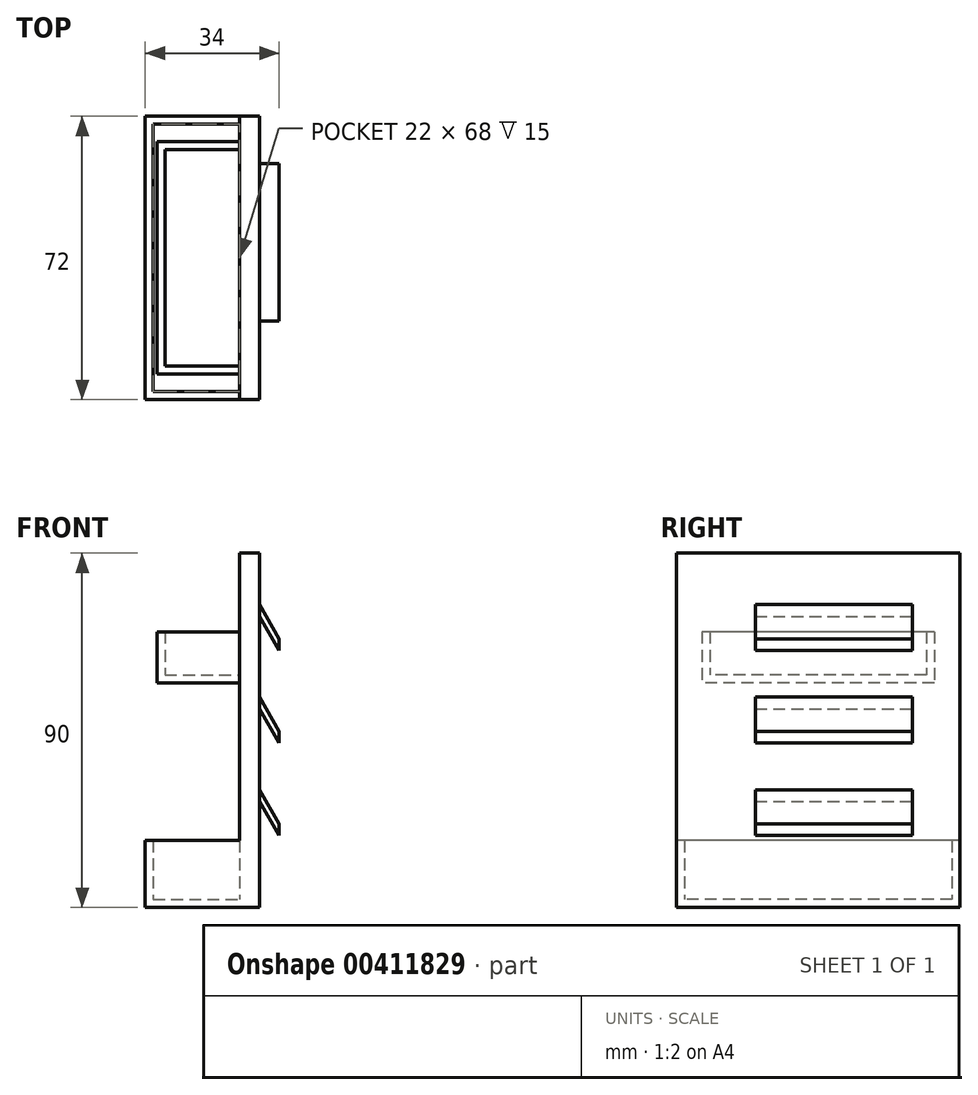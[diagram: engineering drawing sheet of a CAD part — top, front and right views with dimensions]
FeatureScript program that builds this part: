
annotation { "Feature Type Name" : "Feature", "Feature Type Description" : "" }
export const myFeature = defineFeature(function(context is Context, id is Id, definition is map)
    precondition{}
    {
        {
            var Q0;
            Q0=qCreatedBy(makeId("Top.planeOp"),FACE);
            var sketch = newSketch(context, id + "F0", { "sketchPlane" : qUnion([Q0])});
            skLineSegment(sketch, "E0.bottom", {"start": v(2.5, 36) * mm, "end": v(-2.5, 36) * mm});
            skLineSegment(sketch, "E0.top", {"start": v(2.5, -36) * mm, "end": v(-2.5, -36) * mm});
            skLineSegment(sketch, "E0.left", {"start": v(2.5, 36) * mm, "end": v(2.5, -36) * mm});
            skLineSegment(sketch, "E0.right", {"start": v(-2.5, 36) * mm, "end": v(-2.5, -36) * mm});
            skPoint(sketch, "E0.middle", {"position": v(0, 0) * mm});
            skLineSegment(sketch, "E1", {"start": v(-2.5, 36) * mm, "end": v(-26.5, 36) * mm});
            skLineSegment(sketch, "E2", {"start": v(-26.5, 36) * mm, "end": v(-26.5, -36) * mm});
            skLineSegment(sketch, "E3", {"start": v(-26.5, -36) * mm, "end": v(-2.5, -36) * mm});
            skLineSegment(sketch, "E4.0", {"start": v(-24.5, -34) * mm, "end": v(-2.5, -34) * mm});
            skLineSegment(sketch, "E4.1", {"start": v(-24.5, 34) * mm, "end": v(-24.5, -34) * mm});
            skLineSegment(sketch, "E4.2", {"start": v(-2.5, 34) * mm, "end": v(-24.5, 34) * mm});
            skSolve(sketch);
        }
        {
            var Q0;
            Q0=makeQuery(id+"F0.imprint","IMPRINT",FACE,{"disambiguationData":[TD([[makeQuery(id+"F0.imprint","IMPRINT",EDGE,{"derivedFrom":sQuery(id+"F0.wireOp",EDGE,"E0.bottom")}),1.0]])]});
            extrude(context, id + "F1", {"entities" : qUnion([Q0]), "depth" : 90 * mm});
        }
        {
            var Q0;
            {var subQ0=sQuery(id+"F0.wireOp",EDGE,"E1");Q0=makeQuery(id+"F0.imprint","IMPRINT",FACE,{"disambiguationData":[TD([[makeQuery(id+"F0.imprint","IMPRINT",EDGE,{"derivedFrom":subQ0}),1.0]])]});}
            extrude(context, id + "F2", {"entities" : qUnion([Q0]), "operationType" : NewBodyOperationType.ADD, "depth" : 17 * mm});
        }
        {
            var Q0;
            {var subQ0=sQuery(id+"F0.wireOp",EDGE,"E4.0");Q0=makeQuery(id+"F0.imprint","IMPRINT",FACE,{"disambiguationData":[TD([[makeQuery(id+"F0.imprint","IMPRINT",EDGE,{"derivedFrom":subQ0}),1.0]])]});}
            extrude(context, id + "F3", {"entities" : qUnion([Q0]), "operationType" : NewBodyOperationType.ADD, "depth" : 2 * mm});
        }
        {
            var Q0;
            Q0=makeQuery(id+"F2.opExtrude","CAP_FACE",FACE,{"disambiguationData":[OSD([sQuery(id+"F0.wireOp",EDGE,"E0.right"),sQuery(id+"F0.wireOp",EDGE,"E1"),sQuery(id+"F0.wireOp",EDGE,"E2"),sQuery(id+"F0.wireOp",EDGE,"E3"),sQuery(id+"F0.wireOp",EDGE,"E4.0"),sQuery(id+"F0.wireOp",EDGE,"E4.1"),sQuery(id+"F0.wireOp",EDGE,"E4.2")])],"isStart":false});
            cPlane(context, id + "F4", {"entities" : qUnion([Q0]), "cplaneType" : CPlaneType.OFFSET, "offset" : 40 * mm, "width" : 150 * mm, "height" : 150 * mm});
        }
        {
            var Q0;
            Q0=qCreatedBy(id+"F4.planeOp",FACE);
            var sketch = newSketch(context, id + "F5", { "sketchPlane" : qUnion([Q0])});
            skLineSegment(sketch, "E5.0", {"start": v(-2.5, 36) * mm, "end": v(-2.5, -36) * mm});
            skPoint(sketch, "E6.0", {"position": v(-2.5, 0) * mm});
            skLineSegment(sketch, "E7", {"start": v(-2.5, 29.5) * mm, "end": v(-23.5, 29.5) * mm});
            skLineSegment(sketch, "E8", {"start": v(-23.5, 29.5) * mm, "end": v(-23.5, -29.5) * mm});
            skLineSegment(sketch, "E9", {"start": v(-23.5, -29.5) * mm, "end": v(-2.5, -29.5) * mm});
            skLineSegment(sketch, "E10.0", {"start": v(-21.5, -27.5) * mm, "end": v(-2.5, -27.5) * mm});
            skLineSegment(sketch, "E10.1", {"start": v(-21.5, 27.5) * mm, "end": v(-21.5, -27.5) * mm});
            skLineSegment(sketch, "E10.2", {"start": v(-2.5, 27.5) * mm, "end": v(-21.5, 27.5) * mm});
            skPoint(sketch, "E11", {"position": v(-21.5, 0) * mm});
            skSolve(sketch);
        }
        {
            var Q0;
            {var subQ0=sQuery(id+"F5.wireOp",EDGE,"E7");Q0=makeQuery(id+"F5.imprint","IMPRINT",FACE,{"disambiguationData":[TD([[makeQuery(id+"F5.imprint","IMPRINT",EDGE,{"derivedFrom":subQ0}),1.0]])]});}
            extrude(context, id + "F6", {"entities" : qUnion([Q0]), "operationType" : NewBodyOperationType.ADD, "depth" : 13 * mm});
        }
        {
            var Q0;
            {var subQ0=sQuery(id+"F5.wireOp",EDGE,"E10.0");Q0=makeQuery(id+"F5.imprint","IMPRINT",FACE,{"disambiguationData":[TD([[makeQuery(id+"F5.imprint","IMPRINT",EDGE,{"derivedFrom":subQ0}),1.0]])]});}
            extrude(context, id + "F7", {"entities" : qUnion([Q0]), "operationType" : NewBodyOperationType.ADD, "depth" : 2 * mm});
        }
        {
            var Q0;
            Q0=makeQuery(id+"F2.boolean.opBoolean","MERGE",FACE,{"derivedFrom":[makeQuery(id+"F1.opExtrude","SWEPT_FACE",FACE,{"disambiguationData":[OSD([sQuery(id+"F0.wireOp",EDGE,"E0.top")])]}),makeQuery(id+"F2.opExtrude","SWEPT_FACE",FACE,{"disambiguationData":[OSD([sQuery(id+"F0.wireOp",EDGE,"E3")])]})]});
            cPlane(context, id + "F8", {"entities" : qUnion([Q0]), "cplaneType" : CPlaneType.OFFSET, "offset" : 40 * mm, "oppositeDirection" : true, "width" : 150 * mm, "height" : 150 * mm});
        }
        {
            var Q0;
            Q0=qCreatedBy(id+"F8.planeOp",FACE);
            var sketch = newSketch(context, id + "F9", { "sketchPlane" : qUnion([Q0])});
            skLineSegment(sketch, "E12.0", {"start": v(2.5, 90) * mm, "end": v(2.5, 0) * mm});
            skPoint(sketch, "E13.0", {"position": v(2.5, 45) * mm});
            skLineSegment(sketch, "E14", {"start": v(2.5, 76.9) * mm, "end": v(7.5, 68.23) * mm});
            skLineSegment(sketch, "E15", {"start": v(7.5, 68.23) * mm, "end": v(7.5, 65.23) * mm});
            skLineSegment(sketch, "E16", {"start": v(7.5, 65.23) * mm, "end": v(2.5, 73.9) * mm});
            skLineSegment(sketch, "E17.0.1.0", {"start": v(7.5, 44.73) * mm, "end": v(7.5, 41.73) * mm});
            skLineSegment(sketch, "E17.0.1.1", {"start": v(2.5, 53.4) * mm, "end": v(7.5, 44.73) * mm});
            skLineSegment(sketch, "E17.0.1.2", {"start": v(7.5, 41.73) * mm, "end": v(2.5, 50.4) * mm});
            skLineSegment(sketch, "E17.0.2.0", {"start": v(7.5, 21.23) * mm, "end": v(7.5, 18.23) * mm});
            skLineSegment(sketch, "E17.0.2.1", {"start": v(2.5, 29.9) * mm, "end": v(7.5, 21.23) * mm});
            skLineSegment(sketch, "E17.0.2.2", {"start": v(7.5, 18.23) * mm, "end": v(2.5, 26.9) * mm});
            skLineSegment(sketch, "E17.direction1", {"start": v(7.5, 65.23) * mm, "end": v(32.5, 65.23) * mm, "construction": true});
            skLineSegment(sketch, "E17.direction2", {"start": v(7.5, 65.23) * mm, "end": v(7.5, 41.73) * mm, "construction": true});
            skSolve(sketch);
        }
        {
            var Q0;
            {var subQ0=sQuery(id+"F9.wireOp",EDGE,"E14");Q0=makeQuery(id+"F9.imprint","IMPRINT",FACE,{"disambiguationData":[TD([[makeQuery(id+"F9.imprint","IMPRINT",EDGE,{"derivedFrom":subQ0}),-1.0]])]});}
            var Q1;
            Q1=makeQuery(id+"F9.imprint","IMPRINT",FACE,{"disambiguationData":[TD([[makeQuery(id+"F9.imprint","IMPRINT",EDGE,{"derivedFrom":sQuery(id+"F9.wireOp",EDGE,"E17.0.1.0")}),-1.0]])]});
            var Q2;
            Q2=makeQuery(id+"F9.imprint","IMPRINT",FACE,{"disambiguationData":[TD([[makeQuery(id+"F9.imprint","IMPRINT",EDGE,{"derivedFrom":sQuery(id+"F9.wireOp",EDGE,"E17.0.2.0")}),-1.0]])]});
            extrude(context, id + "F10", {"entities" : qUnion([Q0, Q1, Q2]), "operationType" : NewBodyOperationType.ADD, "endBound" : BoundingType.SYMMETRIC, "depth" : 40 * mm});
        }
    });
